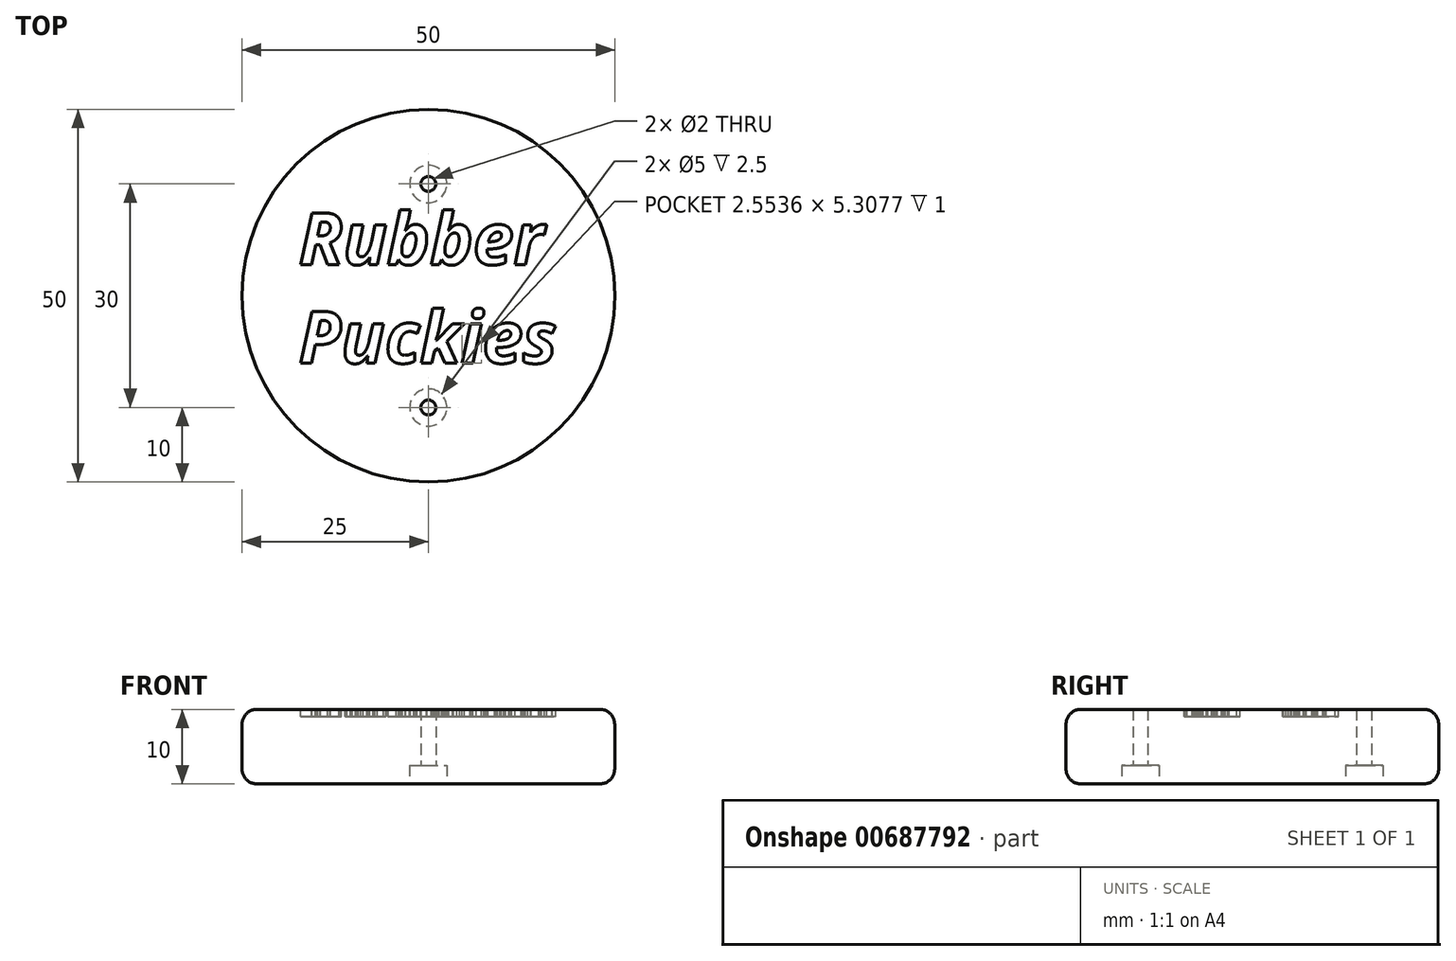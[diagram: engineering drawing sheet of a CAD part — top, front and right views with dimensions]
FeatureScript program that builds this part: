
annotation { "Feature Type Name" : "Feature", "Feature Type Description" : "" }
export const myFeature = defineFeature(function(context is Context, id is Id, definition is map)
    precondition{}
    {
        {
            var Q0;
            Q0=qCreatedBy(makeId("Top.planeOp"),FACE);
            var sketch = newSketch(context, id + "F0", { "sketchPlane" : qUnion([Q0])});
            skCircle(sketch, "E0", {"center": v(0, 0) * mm, "radius": 25 * mm});
            skSolve(sketch);
        }
        {
            var Q0;
            Q0=qSketchRegion(id+"F0",true);
            extrude(context, id + "F1", {"entities" : qUnion([Q0]), "depth" : 10 * mm});
        }
        {
            var Q0;
            Q0=makeQuery(id+"F1.opExtrude","CAP_FACE",FACE,{"disambiguationData":[OSD([sQuery(id+"F0.wireOp",EDGE,"E0")])],"isStart":false});
            var sketch = newSketch(context, id + "F2", { "sketchPlane" : qUnion([Q0])});
            skText(sketch, "E1", { "text": "Rubber\nPuckies", "fontName": "OpenSans-BoldItalic.ttf"});
            const initialGuessF2  = {"E1": [-0.01736, 0.00417, 1, 0, 0.007]};
            skSetInitialGuess(sketch, initialGuessF2);
            skSolve(sketch);
        }
        {
            var Q0;
            Q0=qSketchRegion(id+"F2",true);
            extrude(context, id + "F3", {"entities" : qUnion([Q0]), "operationType" : NewBodyOperationType.REMOVE, "oppositeDirection" : true, "depth" : 1 * mm});
        }
        {
            var Q0;
            Q0=makeQuery(id+"F1.opExtrude","CAP_EDGE",EDGE,{"disambiguationData":[OSD([sQuery(id+"F0.wireOp",EDGE,"E0")])],"isStart":false});
            var Q1;
            Q1=makeQuery(id+"F1.opExtrude","CAP_EDGE",EDGE,{"disambiguationData":[OSD([sQuery(id+"F0.wireOp",EDGE,"E0")])],"isStart":true});
            fillet(context, id + "F4", {"entities" : qUnion([Q0, Q1]), "radius" : 2 * mm, "tangentPropagation" : true, "allowEdgeOverflow" : false});
        }
        {
            var Q0;
            Q0=makeQuery(id+"F1.opExtrude","CAP_FACE",FACE,{"disambiguationData":[OSD([sQuery(id+"F0.wireOp",EDGE,"E0")])],"isStart":true});
            var sketch = newSketch(context, id + "F5", { "sketchPlane" : qUnion([Q0])});
            skPoint(sketch, "E2", {"position": v(0, 15) * mm});
            skPoint(sketch, "E3", {"position": v(0, -15) * mm});
            skSolve(sketch);
        }
        {
            var Q0;
            Q0=sQuery(id+"F5.wireOp",VERTEX,"E2");
            var Q1;
            Q1=sQuery(id+"F5.wireOp",VERTEX,"E3");
            var Q2;
            Q2=makeQuery(id+"F1.opExtrude","SWEPT_BODY",BODY,{"disambiguationData":[OSD([sQuery(id+"F0.wireOp",EDGE,"E0")])]});
            hole(context, id + "F6", {"style" : HoleStyle.C_BORE, "endStyle" : HoleEndStyle.THROUGH, "holeDiameter" : 2 * mm, "cBoreDiameter" : 5 * mm, "cBoreDepth" : 2.5 * mm, "startFromSketch" : true, "locations" : qUnion([Q0, Q1]), "scope" : qUnion([Q2]), "isTappedThrough" : true});
        }
    });
